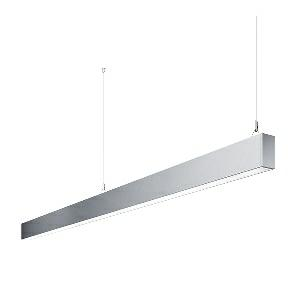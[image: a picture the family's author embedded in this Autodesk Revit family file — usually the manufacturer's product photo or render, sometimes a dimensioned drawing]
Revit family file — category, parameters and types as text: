
# Revit family: dotoo_line_-_dlp_3000_830_d_end_00805854_d386
name_source: partatom
category: Lighting Fixtures
units: mm (PartAtom-declared; Revit-internal decimal feet)

## family parameters
Cut with Voids When Loaded = No
Host = Face
Light Source = No
Part Type = Normal
Room Calculation Point = No
Round Connector Dimension = Use Diameter
Shared = No

## types (1)
- DOTOO.line - DLP 3000/830/D END (1 x LED, 2650 lm, 3000K)
    Apparent Load = 26 VA
    Approval mark = CE
    CIE Flux Codes = 67 91 98 100 100
    Color Rendering = 80-89
    Color Temperature = 3000K
    Control Gear = Electronic ballast
    Default Elevation = 1800 mm
    Description = DLP 3000/830/D|Suspended luminaire|light source: LED|connected load: 220-240 V, 50/60 Hz|Power consumption: approx. 26 W|standby: approx. 0,15|luminous flux: 2650 lm|luminous efficacy: 101 lm/W|light distribution: Direct|direct ratio: approx. 100 %|colour temperature: Warm white, ca. 3000 K|color rendering index (CRI): >= 80|chromaticity tolerance:  3 SDCM|System of protection: IP 40|technology: Continuously dimmable|luminaire body|material: Sectional aluminium|colour: Silver|lamp cover: Acrylic (PMMA), Clear|mains lead: 1,0 m With free stranded wires|Fastening: Steel cable 0.3 - 0.7 m|glare control: Prism aperture|luminance(L65): <= 3000 cd/m|unified glare rating(4H 8H): <=  19|special features: DALI Load 1x, TouchDIM - dimming via standard switch, Through-wired, up to 18 m on one mains connection, Flicker-free, Suitable as emergency lighting, Mechanical and electrical connection of the individual modules without tools|
    Frequency = 50 Hz
    Height = 110 mm
    Lamp = 1 x LED
    Lamp Light Flux = 2650 lm
    Lamp count = 1
    Length = 2250 mm
    Luminous efficacy = 102 lm/W
    Manufacturer = Waldmann
    ModVariant = No
    Model = 00805854
    Mounting Place = Ceiling
    Mounting Type = Pendant
    Number of Poles = 1
    OnlyDefault = Yes
    Power Factor = 1
    Product Name = DOTOO.line - DLP 3000/830/D END
    Product group = Suspended luminaire
    ProductGroupID = 9
    Protection Class = Protection class I
    Protection Degree = IP 40
    RLX_Detail_Level = 1
    RLX_Emergency_Light_Flux = 0 lm
    RLX_Emergency_Type = 0
    RLX_Emergency_Type_DB = No
    RlxData = <blob elided: 23077 chars, md5=4d2ae2f0>
    Socket = socket
    Standby Power = 0 W
    System Light Flux = 2650 lm
    System Power = 26 W
    Type Comments = Product without accessories
    Type Image = 113318000-00692621.jpg
    URL = http://relux.com
    VarID = ---
    Voltage = 230 V
    Voltage Range = 220-240 V
    Weight = 0.00 kg
    Width = 60 mm  [stored 0.19685 ft]

note: [stored X ft] marks values corroborated as IEEE doubles in the binary element streams (Revit-internal decimal feet)

## geometry (parser evidence)
native form markers: Blend x4, Sweep x12
no freeform markers — native parametric forms only
